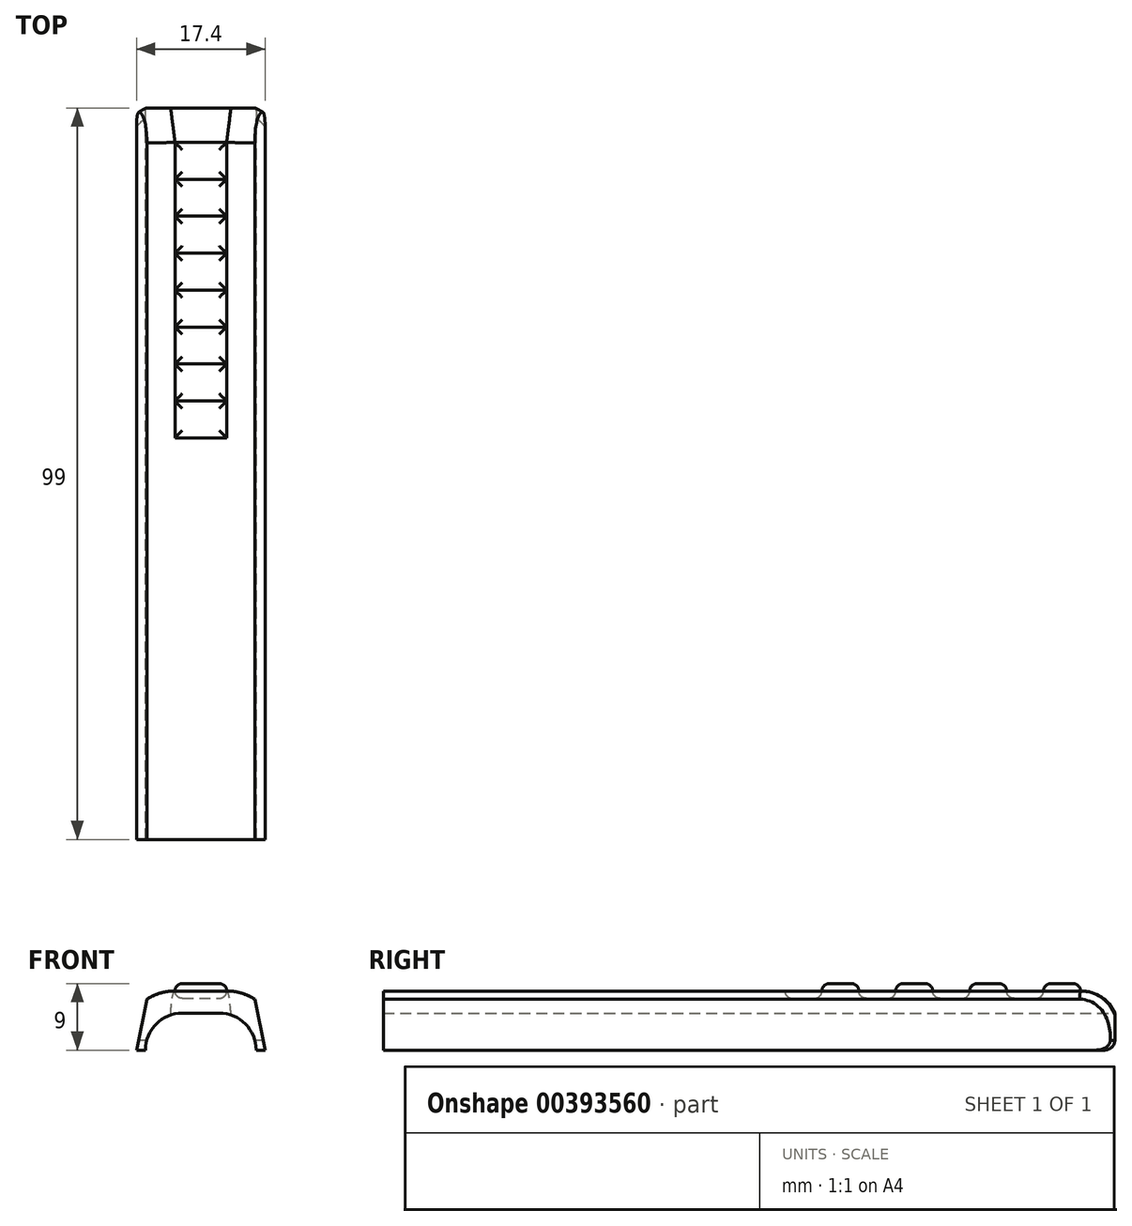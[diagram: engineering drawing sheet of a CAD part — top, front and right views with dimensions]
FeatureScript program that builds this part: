
annotation { "Feature Type Name" : "Feature", "Feature Type Description" : "" }
export const myFeature = defineFeature(function(context is Context, id is Id, definition is map)
    precondition{}
    {
        {
            var Q0;
            Q0=qCreatedBy(makeId("Front.planeOp"),FACE);
            var sketch = newSketch(context, id + "F0", { "sketchPlane" : qUnion([Q0])});
            skLineSegment(sketch, "E0.bottom", {"start": v(8.35, 10.13) * mm, "end": v(8.35, -14.87) * mm});
            skLineSegment(sketch, "E0.top", {"start": v(-6.65, 10.13) * mm, "end": v(-6.65, -14.87) * mm});
            skLineSegment(sketch, "E0.left", {"start": v(3.35, 15.13) * mm, "end": v(-1.65, 15.13) * mm});
            skLineSegment(sketch, "E0.right", {"start": v(3.35, -19.87) * mm, "end": v(-1.65, -19.87) * mm});
            skLineSegment(sketch, "E1.bottom", {"start": v(11.35, 11.13) * mm, "end": v(11.35, -15.87) * mm});
            skLineSegment(sketch, "E1.top", {"start": v(-9.65, 11.13) * mm, "end": v(-9.65, -15.87) * mm});
            skLineSegment(sketch, "E1.left", {"start": v(4.35, 18.13) * mm, "end": v(-2.65, 18.13) * mm});
            skLineSegment(sketch, "E1.right", {"start": v(4.35, -22.87) * mm, "end": v(-2.65, -22.87) * mm});
            skPoint(sketch, "E2.visualSharp", {"position": v(11.35, -22.87) * mm});
            skArc(sketch, "E2.filletArc", {"start": v(4.35, -22.87) * mm, "mid": v(9.3, -20.82) * mm, "end": v(11.35, -15.87) * mm});
            skPoint(sketch, "E3.visualSharp", {"position": v(-9.65, -22.87) * mm});
            skArc(sketch, "E3.filletArc", {"start": v(-9.65, -15.87) * mm, "mid": v(-7.6, -20.82) * mm, "end": v(-2.65, -22.87) * mm});
            skPoint(sketch, "E4.visualSharp", {"position": v(-9.65, 18.13) * mm});
            skArc(sketch, "E4.filletArc", {"start": v(-2.65, 18.13) * mm, "mid": v(-7.6, 16.08) * mm, "end": v(-9.65, 11.13) * mm});
            skPoint(sketch, "E5.visualSharp", {"position": v(11.35, 18.13) * mm});
            skArc(sketch, "E5.filletArc", {"start": v(11.35, 11.13) * mm, "mid": v(9.3, 16.08) * mm, "end": v(4.35, 18.13) * mm});
            skPoint(sketch, "E6.visualSharp", {"position": v(8.35, -19.87) * mm});
            skArc(sketch, "E6.filletArc", {"start": v(3.35, -19.87) * mm, "mid": v(6.9, -18.4) * mm, "end": v(8.35, -14.87) * mm});
            skPoint(sketch, "E7.visualSharp", {"position": v(-6.65, -19.87) * mm});
            skArc(sketch, "E7.filletArc", {"start": v(-6.65, -14.87) * mm, "mid": v(-5.18, -18.4) * mm, "end": v(-1.65, -19.87) * mm});
            skPoint(sketch, "E8.visualSharp", {"position": v(-6.65, 15.13) * mm});
            skArc(sketch, "E8.filletArc", {"start": v(-1.65, 15.13) * mm, "mid": v(-5.18, 13.67) * mm, "end": v(-6.65, 10.13) * mm});
            skPoint(sketch, "E9.visualSharp", {"position": v(8.35, 15.13) * mm});
            skArc(sketch, "E9.filletArc", {"start": v(8.35, 10.13) * mm, "mid": v(6.9, 13.67) * mm, "end": v(3.35, 15.13) * mm});
            skLineSegment(sketch, "E10", {"start": v(-6.65, 10.13) * mm, "end": v(-7.85, 10.13) * mm});
            skLineSegment(sketch, "E11", {"start": v(8.35, 10.13) * mm, "end": v(9.55, 10.13) * mm});
            skLineSegment(sketch, "E12", {"start": v(-6.45, 17.01) * mm, "end": v(-7.85, 10.13) * mm});
            skLineSegment(sketch, "E13", {"start": v(8.15, 17.01) * mm, "end": v(9.55, 10.13) * mm});
            skLineSegment(sketch, "E14", {"start": v(-6.65, 10.13) * mm, "end": v(-6.65, 15.13) * mm});
            skLineSegment(sketch, "E15", {"start": v(8.35, 10.13) * mm, "end": v(8.35, 15.13) * mm});
            skLineSegment(sketch, "E16.left", {"start": v(-1.65, 15.13) * mm, "end": v(3.35, 15.13) * mm});
            skPoint(sketch, "E17.visualSharp", {"position": v(1.01, 15.61) * mm});
            skPoint(sketch, "E18.visualSharp", {"position": v(-6.45, 14.62) * mm});
            skLineSegment(sketch, "E19", {"start": v(8.35, 15.13) * mm, "end": v(8.35, 35.9) * mm, "construction": true});
            skLineSegment(sketch, "E20", {"start": v(-6.65, 15.13) * mm, "end": v(-6.65, 19.52) * mm, "construction": true});
            skSolve(sketch);
        }
        {
            var Q0;
            {var subQ1=sQuery(id+"F0.wireOp",EDGE,"E1.left");Q0=makeQuery(id+"F0.imprint","IMPRINT",FACE,{"disambiguationData":[TD([[makeQuery(id+"F0.imprint","IMPRINT",EDGE,{"derivedFrom":subQ1}),1.0]])]});}
            extrude(context, id + "F1", {"entities" : qUnion([Q0]), "depth" : 84 * mm});
        }
        {
            var Q0;
            Q0=makeQuery(id+"F1.opExtrude","CAP_FACE",FACE,{"disambiguationData":[OSD([sQuery(id+"F0.wireOp",EDGE,"E1.left"),sQuery(id+"F0.wireOp",EDGE,"E4.filletArc"),sQuery(id+"F0.wireOp",EDGE,"E5.filletArc"),sQuery(id+"F0.wireOp",EDGE,"E8.filletArc"),sQuery(id+"F0.wireOp",EDGE,"E9.filletArc"),sQuery(id+"F0.wireOp",EDGE,"E10"),sQuery(id+"F0.wireOp",EDGE,"E11"),sQuery(id+"F0.wireOp",EDGE,"E12"),sQuery(id+"F0.wireOp",EDGE,"E13"),sQuery(id+"F0.wireOp",EDGE,"E16.left")])],"isStart":true});
            extrude(context, id + "F2", {"entities" : qUnion([Q0]), "operationType" : NewBodyOperationType.ADD, "depth" : 15 * mm});
        }
        {
            var Q0;
            Q0=makeQuery(id+"F2.opExtrude","CAP_EDGE",EDGE,{"disambiguationData":[OSD([sQuery(id+"F0.wireOp",EDGE,"E1.left")])],"isStart":false});
            fillet(context, id + "F3", {"entities" : qUnion([Q0]), "radius" : 5 * mm, "tangentPropagation" : true, "allowEdgeOverflow" : false});
        }
        {
            var Q0;
            {var subQ0=sQuery(id+"F0.wireOp",EDGE,"E10");Q0=makeQuery(id+"F3.opFillet","BLEND_EDGE",EDGE,{"blendedFrom":[makeQuery(id+"F2.opExtrude","CAP_EDGE",EDGE,{"disambiguationData":[OSD([sQuery(id+"F0.wireOp",EDGE,"E4.filletArc")])],"isStart":false}),makeQuery(id+"F2.boolean.opBoolean","MERGE",FACE,{"derivedFrom":[makeQuery(id+"F1.opExtrude","SWEPT_FACE",FACE,{"disambiguationData":[OSD([subQ0])]}),makeQuery(id+"F2.opExtrude","SWEPT_FACE",FACE,{"disambiguationData":[OSD([subQ0])]})]})],"blendedInto":[makeQuery(id+"F2.boolean.opBoolean","MERGE",FACE,{"derivedFrom":[makeQuery(id+"F1.opExtrude","SWEPT_FACE",FACE,{"disambiguationData":[OSD([subQ0])]}),makeQuery(id+"F2.opExtrude","SWEPT_FACE",FACE,{"disambiguationData":[OSD([subQ0])]})]})]});}
            var Q1;
            {var subQ0=sQuery(id+"F0.wireOp",EDGE,"E11");Q1=makeQuery(id+"F3.opFillet","BLEND_EDGE",EDGE,{"blendedFrom":[makeQuery(id+"F2.opExtrude","CAP_EDGE",EDGE,{"disambiguationData":[OSD([sQuery(id+"F0.wireOp",EDGE,"E5.filletArc")])],"isStart":false}),makeQuery(id+"F2.boolean.opBoolean","MERGE",FACE,{"derivedFrom":[makeQuery(id+"F1.opExtrude","SWEPT_FACE",FACE,{"disambiguationData":[OSD([subQ0])]}),makeQuery(id+"F2.opExtrude","SWEPT_FACE",FACE,{"disambiguationData":[OSD([subQ0])]})]})],"blendedInto":[makeQuery(id+"F2.boolean.opBoolean","MERGE",FACE,{"derivedFrom":[makeQuery(id+"F1.opExtrude","SWEPT_FACE",FACE,{"disambiguationData":[OSD([subQ0])]}),makeQuery(id+"F2.opExtrude","SWEPT_FACE",FACE,{"disambiguationData":[OSD([subQ0])]})]})]});}
            fillet(context, id + "F4", {"entities" : qUnion([Q0, Q1]), "radius" : 1.2 * mm, "tangentPropagation" : true, "allowEdgeOverflow" : false});
        }
        {
            var Q0;
            {var subQ0=sQuery(id+"F0.wireOp",EDGE,"E1.left");Q0=makeQuery(id+"F2.boolean.opBoolean","MERGE",FACE,{"derivedFrom":[makeQuery(id+"F1.opExtrude","SWEPT_FACE",FACE,{"disambiguationData":[OSD([subQ0])]}),makeQuery(id+"F2.opExtrude","SWEPT_FACE",FACE,{"disambiguationData":[OSD([subQ0])]})]});}
            var sketch = newSketch(context, id + "F5", { "sketchPlane" : qUnion([Q0])});
            skLineSegment(sketch, "E21.bottom", {"start": v(-2.65, 10.35) * mm, "end": v(4.35, 10.35) * mm});
            skLineSegment(sketch, "E21.top", {"start": v(-2.65, -29.65) * mm, "end": v(4.35, -29.65) * mm});
            skLineSegment(sketch, "E21.left", {"start": v(-2.65, 10.35) * mm, "end": v(-2.65, -29.65) * mm});
            skLineSegment(sketch, "E21.right", {"start": v(4.35, 10.35) * mm, "end": v(4.35, -29.65) * mm});
            skLineSegment(sketch, "E22", {"start": v(-2.65, 0.35) * mm, "end": v(4.35, 0.35) * mm});
            skLineSegment(sketch, "E23", {"start": v(-2.65, -4.65) * mm, "end": v(4.35, -4.65) * mm});
            skLineSegment(sketch, "E24", {"start": v(-2.65, -14.65) * mm, "end": v(4.35, -14.65) * mm});
            skLineSegment(sketch, "E25", {"start": v(-2.65, -9.65) * mm, "end": v(4.35, -9.65) * mm});
            skLineSegment(sketch, "E26", {"start": v(-2.65, -19.65) * mm, "end": v(4.35, -19.65) * mm});
            skLineSegment(sketch, "E27", {"start": v(-2.65, 5.35) * mm, "end": v(4.35, 5.35) * mm});
            skLineSegment(sketch, "E28", {"start": v(-2.65, -24.65) * mm, "end": v(4.35, -24.65) * mm});
            skSolve(sketch);
        }
        {
            var Q0;
            {var subQ0=sQuery(id+"F5.wireOp",EDGE,"E21.bottom");Q0=makeQuery(id+"F5.imprint","IMPRINT",FACE,{"disambiguationData":[TD([[makeQuery(id+"F5.imprint","IMPRINT",EDGE,{"derivedFrom":subQ0}),-1.0]])]});}
            var Q1;
            {var subQ0=sQuery(id+"F5.wireOp",EDGE,"E22");Q1=makeQuery(id+"F5.imprint","IMPRINT",FACE,{"disambiguationData":[TD([[makeQuery(id+"F5.imprint","IMPRINT",EDGE,{"derivedFrom":subQ0}),-1.0]])]});}
            var Q2;
            {var subQ0=sQuery(id+"F5.wireOp",EDGE,"E24");Q2=makeQuery(id+"F5.imprint","IMPRINT",FACE,{"disambiguationData":[TD([[makeQuery(id+"F5.imprint","IMPRINT",EDGE,{"derivedFrom":subQ0}),1.0]])]});}
            var Q3;
            {var subQ0=sQuery(id+"F5.wireOp",EDGE,"E26");Q3=makeQuery(id+"F5.imprint","IMPRINT",FACE,{"disambiguationData":[TD([[makeQuery(id+"F5.imprint","IMPRINT",EDGE,{"derivedFrom":subQ0}),-1.0]])]});}
            extrude(context, id + "F6", {"entities" : qUnion([Q0, Q1, Q2, Q3]), "operationType" : NewBodyOperationType.ADD, "depth" : 1 * mm});
        }
        {
            var Q0;
            {var subQ2=sQuery(id+"F5.wireOp",EDGE,"E22");var subQ7=sQuery(id+"F0.wireOp",EDGE,"E1.left");var subQ8=makeQuery(id+"F2.boolean.opBoolean","MERGE",FACE,{"derivedFrom":[makeQuery(id+"F1.opExtrude","SWEPT_FACE",FACE,{"disambiguationData":[OSD([subQ7])]}),makeQuery(id+"F2.opExtrude","SWEPT_FACE",FACE,{"disambiguationData":[OSD([subQ7])]})]});Q0=makeQuery(id+"F6.boolean.opBoolean","SPLIT",FACE,{"disambiguationData":[TD([makeQuery(id+"F6.opExtrude","SWEPT_FACE",FACE,{"disambiguationData":[OSD([subQ2])]})])],"derivedFrom":subQ8});}
            var Q1;
            {var subQ4=sQuery(id+"F5.wireOp",EDGE,"E23");var subQ8=sQuery(id+"F0.wireOp",EDGE,"E1.left");Q1=makeQuery(id+"F6.boolean.opBoolean","SPLIT",FACE,{"disambiguationData":[TD([makeQuery(id+"F6.opExtrude","SWEPT_FACE",FACE,{"disambiguationData":[OSD([subQ4])]})])],"derivedFrom":makeQuery(id+"F2.boolean.opBoolean","MERGE",FACE,{"derivedFrom":[makeQuery(id+"F1.opExtrude","SWEPT_FACE",FACE,{"disambiguationData":[OSD([subQ8])]}),makeQuery(id+"F2.opExtrude","SWEPT_FACE",FACE,{"disambiguationData":[OSD([subQ8])]})]})});}
            var Q2;
            {var subQ3=sQuery(id+"F5.wireOp",EDGE,"E24");var subQ8=sQuery(id+"F0.wireOp",EDGE,"E1.left");Q2=makeQuery(id+"F6.boolean.opBoolean","SPLIT",FACE,{"disambiguationData":[TD([makeQuery(id+"F6.opExtrude","SWEPT_FACE",FACE,{"disambiguationData":[OSD([subQ3])]})])],"derivedFrom":makeQuery(id+"F2.boolean.opBoolean","MERGE",FACE,{"derivedFrom":[makeQuery(id+"F1.opExtrude","SWEPT_FACE",FACE,{"disambiguationData":[OSD([subQ8])]}),makeQuery(id+"F2.opExtrude","SWEPT_FACE",FACE,{"disambiguationData":[OSD([subQ8])]})]})});}
            var Q3;
            {var subQ0=sQuery(id+"F5.wireOp",EDGE,"E21.top");Q3=makeQuery(id+"F5.imprint","IMPRINT",FACE,{"disambiguationData":[TD([[makeQuery(id+"F5.imprint","IMPRINT",EDGE,{"derivedFrom":subQ0}),1.0]])]});}
            extrude(context, id + "F7", {"entities" : qUnion([Q0, Q1, Q2, Q3]), "operationType" : NewBodyOperationType.REMOVE, "oppositeDirection" : true, "depth" : 1 * mm});
        }
        {
            var Q0;
            Q0=makeQuery(id+"F6.opExtrude","CAP_FACE",FACE,{"disambiguationData":[OSD([sQuery(id+"F5.wireOp",EDGE,"E21.left"),sQuery(id+"F5.wireOp",EDGE,"E21.right"),sQuery(id+"F5.wireOp",EDGE,"E26"),sQuery(id+"F5.wireOp",EDGE,"E28")])],"isStart":false});
            var Q1;
            Q1=makeQuery(id+"F6.opExtrude","CAP_FACE",FACE,{"disambiguationData":[OSD([sQuery(id+"F5.wireOp",EDGE,"E21.left"),sQuery(id+"F5.wireOp",EDGE,"E21.right"),sQuery(id+"F5.wireOp",EDGE,"E24"),sQuery(id+"F5.wireOp",EDGE,"E25")])],"isStart":false});
            var Q2;
            Q2=makeQuery(id+"F6.opExtrude","CAP_FACE",FACE,{"disambiguationData":[OSD([sQuery(id+"F5.wireOp",EDGE,"E21.left"),sQuery(id+"F5.wireOp",EDGE,"E21.right"),sQuery(id+"F5.wireOp",EDGE,"E22"),sQuery(id+"F5.wireOp",EDGE,"E23")])],"isStart":false});
            var Q3;
            Q3=makeQuery(id+"F6.opExtrude","CAP_FACE",FACE,{"disambiguationData":[OSD([sQuery(id+"F5.wireOp",EDGE,"E21.bottom"),sQuery(id+"F5.wireOp",EDGE,"E21.left"),sQuery(id+"F5.wireOp",EDGE,"E21.right"),sQuery(id+"F5.wireOp",EDGE,"E27")])],"isStart":false});
            var Q4;
            {var subQ2=sQuery(id+"F5.wireOp",EDGE,"E22");var subQ7=sQuery(id+"F0.wireOp",EDGE,"E1.left");var subQ8=makeQuery(id+"F2.boolean.opBoolean","MERGE",FACE,{"derivedFrom":[makeQuery(id+"F1.opExtrude","SWEPT_FACE",FACE,{"disambiguationData":[OSD([subQ7])]}),makeQuery(id+"F2.opExtrude","SWEPT_FACE",FACE,{"disambiguationData":[OSD([subQ7])]})]});Q4=makeQuery(id+"F7.boolean.opBoolean","COPY",FACE,{"derivedFrom":makeQuery(id+"F7.opExtrude","CAP_FACE",FACE,{"disambiguationData":[OSD([subQ7]),TDD([makeQuery(id+"F6.boolean.opBoolean","SPLIT",FACE,{"disambiguationData":[TD([makeQuery(id+"F6.opExtrude","SWEPT_FACE",FACE,{"disambiguationData":[OSD([subQ2])]})])],"derivedFrom":subQ8})])],"isStart":false})});}
            var Q5;
            {var subQ4=sQuery(id+"F5.wireOp",EDGE,"E23");var subQ8=sQuery(id+"F0.wireOp",EDGE,"E1.left");Q5=makeQuery(id+"F7.boolean.opBoolean","COPY",FACE,{"derivedFrom":makeQuery(id+"F7.opExtrude","CAP_FACE",FACE,{"disambiguationData":[OSD([subQ8]),TDD([makeQuery(id+"F6.boolean.opBoolean","SPLIT",FACE,{"disambiguationData":[TD([makeQuery(id+"F6.opExtrude","SWEPT_FACE",FACE,{"disambiguationData":[OSD([subQ4])]})])],"derivedFrom":makeQuery(id+"F2.boolean.opBoolean","MERGE",FACE,{"derivedFrom":[makeQuery(id+"F1.opExtrude","SWEPT_FACE",FACE,{"disambiguationData":[OSD([subQ8])]}),makeQuery(id+"F2.opExtrude","SWEPT_FACE",FACE,{"disambiguationData":[OSD([subQ8])]})]})})])],"isStart":false})});}
            var Q6;
            {var subQ3=sQuery(id+"F5.wireOp",EDGE,"E24");var subQ8=sQuery(id+"F0.wireOp",EDGE,"E1.left");Q6=makeQuery(id+"F7.boolean.opBoolean","COPY",FACE,{"derivedFrom":makeQuery(id+"F7.opExtrude","CAP_FACE",FACE,{"disambiguationData":[OSD([subQ8]),TDD([makeQuery(id+"F6.boolean.opBoolean","SPLIT",FACE,{"disambiguationData":[TD([makeQuery(id+"F6.opExtrude","SWEPT_FACE",FACE,{"disambiguationData":[OSD([subQ3])]})])],"derivedFrom":makeQuery(id+"F2.boolean.opBoolean","MERGE",FACE,{"derivedFrom":[makeQuery(id+"F1.opExtrude","SWEPT_FACE",FACE,{"disambiguationData":[OSD([subQ8])]}),makeQuery(id+"F2.opExtrude","SWEPT_FACE",FACE,{"disambiguationData":[OSD([subQ8])]})]})})])],"isStart":false})});}
            var Q7;
            Q7=makeQuery(id+"F7.boolean.opBoolean","COPY",FACE,{"derivedFrom":makeQuery(id+"F7.opExtrude","CAP_FACE",FACE,{"disambiguationData":[OSD([sQuery(id+"F5.wireOp",EDGE,"E21.top"),sQuery(id+"F5.wireOp",EDGE,"E21.left"),sQuery(id+"F5.wireOp",EDGE,"E21.right"),sQuery(id+"F5.wireOp",EDGE,"E28")])],"isStart":false})});
            fillet(context, id + "F8", {"entities" : qUnion([Q0, Q1, Q2, Q3, Q4, Q5, Q6, Q7]), "radius" : 1 * mm, "tangentPropagation" : true, "allowEdgeOverflow" : false});
        }
    });
